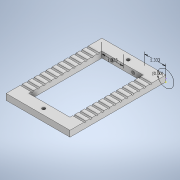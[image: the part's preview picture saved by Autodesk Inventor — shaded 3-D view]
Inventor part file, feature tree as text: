
AUTODESK INVENTOR PART (.ipt)
format: ipt  version: 2020 (Build 240168000, 168)  size: 196,096 bytes
history: native  units: in
note: dims shown in document units (in); Inventor stores cm internally (conversion verified against a paired STEP export)
features: sketch x6, hole x4, extrude x3
ambient origin geometry x8: Origin, YZ Plane, XZ Plane, XY Plane, X Axis, Y Axis, Z Axis, Center Point
bodies: Solid1 (feature_tree)
feature tree (13):
  extrude  "Extrusion1"  Depth=6.0in
  extrude  "Extrusion2"  Depth=0.375in
  extrude  "Extrusion3"  Depth=1.0in
  sketch  "Sketch4"  dims[d7=0.375in d8=0.0in d11=0.9375in]
  hole  "Hole1"  [1 undecoded]
  hole  "Hole2"  [1 undecoded]
  sketch  "Sketch5"  dims[d12=0.125in d13=4.7244in d15=0.375in d16=0.3937in d18=1.0in]
  sketch  "Sketch6"  dims[d20=4.25in d21=0.0in d22=1.333in d23=1.333in d24=0.0in d25=0.196in d26=0.5in d27=0.375in d28=0.25in d29=0.5635in d30=1.0in d31=0.0in d32=0.196in d33=0.5in d34=0.375in d35=0.25in d36=0.5635in d37=1.0in d38=0.0in d39=0.196in d40=0.5in d41=0.375in d42=0.25in d43=0.5635in d44=1.0in d45=0.0in d46=0.196in d47=0.5in d48=0.375in d49=0.25in d50=0.5635in d51=1.0in d52=0.0in]
  hole  "Hole3"  [1 undecoded]
  hole  "Hole4"  [1 undecoded]
  sketch  "Sketch1"  dims[d0=4.0in d1=6.0in]
  sketch  "Sketch2"  dims[d2=0.375in d3=0.0in d4=1.0in]
  sketch  "Sketch3"  dims[d5=135.0deg d6=1.0in]
note: 4 required parameter values undecoded (feature->parameter linkage not recoverable at this tier; creation-order binding heuristic only, values carry confidence <= 0.55)
